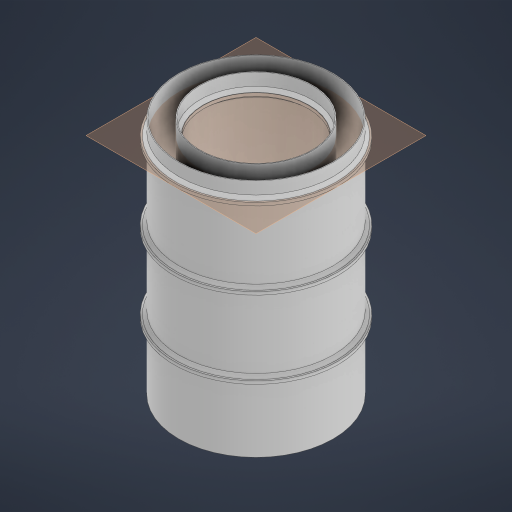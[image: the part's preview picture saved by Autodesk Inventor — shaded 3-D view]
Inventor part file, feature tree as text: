
AUTODESK INVENTOR PART (.ipt)
format: ipt  version: 2024 (Build 280153000, 153)  size: 381,952 bytes
history: native  units: mm
features: sketch x6, extrude x5, chamfer x3, shell x1, plane x1, pattern_linear x1
ambient origin geometry x8: Origin, YZ Plane, XZ Plane, XY Plane, X Axis, Y Axis, Z Axis, Center Point
bodies: Solid1 (feature_tree)
feature tree (17):
  extrude  "Extrusion1"  Depth=200.0mm
  shell  "Shell1"  Thickness=310.0mm
  sketch  "Sketch2"  dims[d4=1.0mm d5=360.0mm d7=360.0deg]
  extrude  "Extrusion2"  Depth=360.0mm TaperAngle=360.0deg
  extrude  "Extrusion3"  Depth=147.0mm
  extrude  "Extrusion4"  Depth=14.0mm TaperAngle=0.0deg
  chamfer  "Chamfer1"  Distance=7.0mm
  chamfer  "Chamfer2"  Distance=1.5mm Angle=45.0deg
  plane  "Work Plane1"
  extrude  "Extrusion5"  [1 undecoded]
  chamfer  "Chamfer3"  Distance=4.0mm
  pattern_linear  "Rectangular Pattern1"  Count1=3  [1 undecoded]
  sketch  "Sketch1"  dims[d0=145.0mm d1=200.0mm d2=310.0mm d3=0.0mm]
  sketch  "Sketch4"  dims[d9=320.0mm d10=0.0mm d11=147.0mm]
  sketch  "Sketch5"  dims[d12=198.0mm d13=14.0mm d14=0.0mm d15=7.0mm d16=0.0mm d17=1.5mm d18=2.0mm d19=45.0deg]
  sketch  "Sketch6"  dims[d20=2.0mm d21=2.0mm d22=45.0deg d23=-20.0mm d24=4.0mm d25=0.0mm]
  sketch  "Sketch7"  dims[d26=4.0mm d27=2.0mm d28=45.0deg d29=30.0mm d31=100.0mm]
note: 2 required parameter values undecoded (feature->parameter linkage not recoverable at this tier; creation-order binding heuristic only, values carry confidence <= 0.55)
